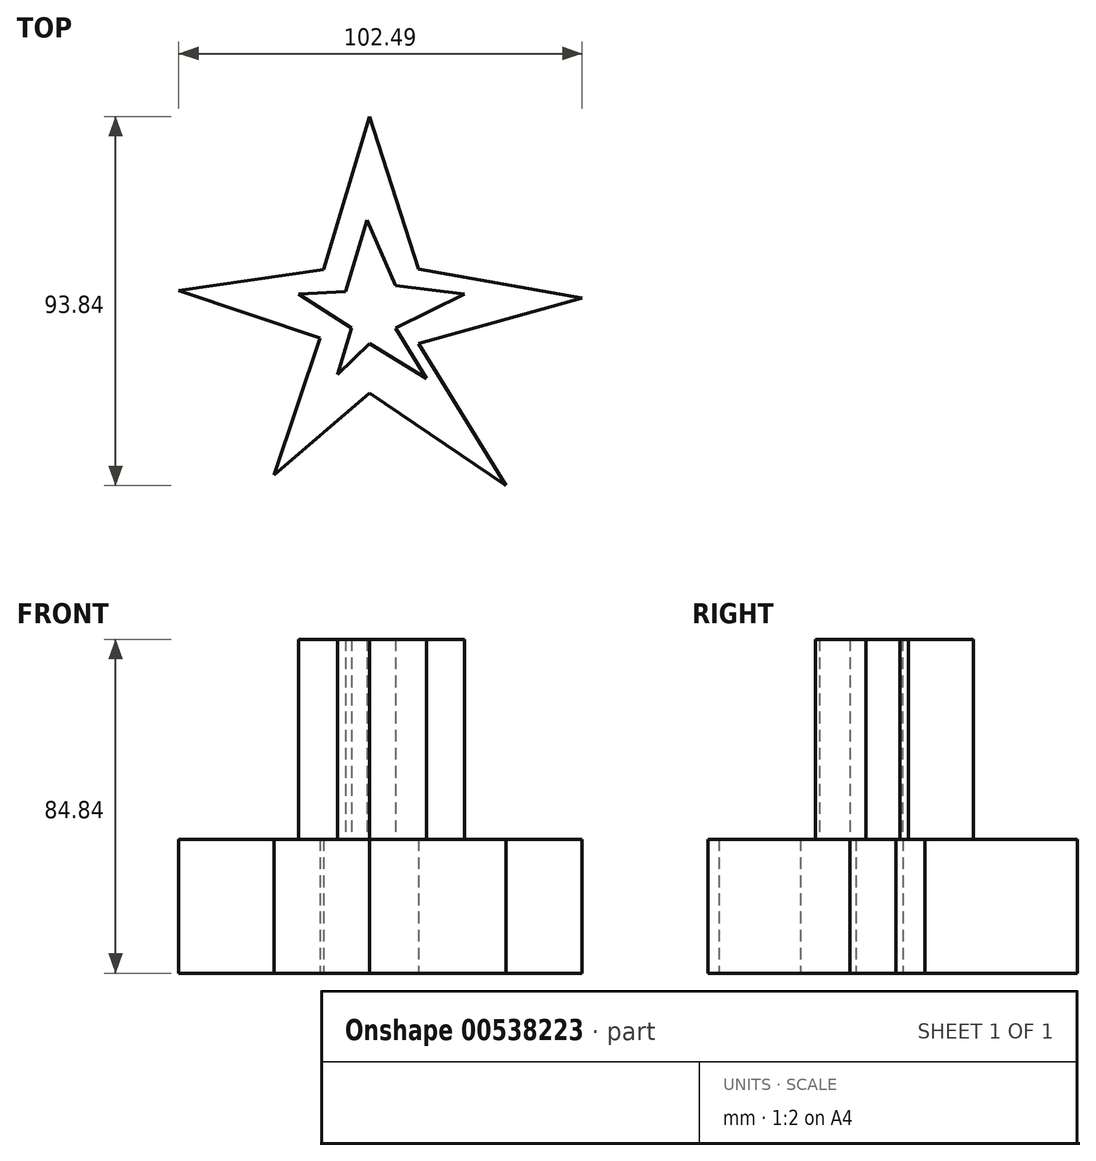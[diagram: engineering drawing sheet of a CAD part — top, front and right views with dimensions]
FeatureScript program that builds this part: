
annotation { "Feature Type Name" : "Feature", "Feature Type Description" : "" }
export const myFeature = defineFeature(function(context is Context, id is Id, definition is map)
    precondition{}
    {
        {
            var Q0;
            Q0=qCreatedBy(makeId("Top.planeOp"),FACE);
            var sketch = newSketch(context, id + "F0", { "sketchPlane" : qUnion([Q0])});
            skLineSegment(sketch, "E0", {"start": v(-62.37, 44.98) * mm, "end": v(-62.37, 49.04) * mm});
            skLineSegment(sketch, "E1", {"start": v(-11.71, 23.03) * mm, "end": v(0, 61.94) * mm});
            skLineSegment(sketch, "E2", {"start": v(0, 61.94) * mm, "end": v(12.43, 23.2) * mm});
            skLineSegment(sketch, "E3", {"start": v(12.43, 23.2) * mm, "end": v(54.01, 15.77) * mm});
            skLineSegment(sketch, "E4", {"start": v(54.01, 15.77) * mm, "end": v(12.43, 4.18) * mm});
            skLineSegment(sketch, "E5", {"start": v(12.43, 4.18) * mm, "end": v(34.64, -31.9) * mm});
            skLineSegment(sketch, "E6", {"start": v(34.64, -31.9) * mm, "end": v(0, -8.39) * mm});
            skLineSegment(sketch, "E7", {"start": v(0, -8.39) * mm, "end": v(-24.2, -29.13) * mm});
            skLineSegment(sketch, "E8", {"start": v(-24.2, -29.13) * mm, "end": v(-12.56, 5.63) * mm});
            skLineSegment(sketch, "E9", {"start": v(-12.56, 5.63) * mm, "end": v(-48.48, 17.66) * mm});
            skLineSegment(sketch, "E10", {"start": v(-48.48, 17.66) * mm, "end": v(-11.71, 23.03) * mm});
            skSolve(sketch);
        }
        {
            var Q0;
            Q0=makeQuery(id+"F0.imprint","IMPRINT",FACE,{"disambiguationData":[TD([[makeQuery(id+"F0.imprint","IMPRINT",EDGE,{"derivedFrom":sQuery(id+"F0.wireOp",EDGE,"E1")}),-1.0]])]});
            extrude(context, id + "F1", {"entities" : qUnion([Q0]), "depth" : 34.04 * mm, "offsetDistance" : 25.4 * mm});
        }
        {
            var Q0;
            Q0=makeQuery(id+"F1.opExtrude","CAP_FACE",FACE,{"disambiguationData":[OSD([sQuery(id+"F0.wireOp",EDGE,"E1"),sQuery(id+"F0.wireOp",EDGE,"E2"),sQuery(id+"F0.wireOp",EDGE,"E3"),sQuery(id+"F0.wireOp",EDGE,"E4"),sQuery(id+"F0.wireOp",EDGE,"E5"),sQuery(id+"F0.wireOp",EDGE,"E6"),sQuery(id+"F0.wireOp",EDGE,"E7"),sQuery(id+"F0.wireOp",EDGE,"E8"),sQuery(id+"F0.wireOp",EDGE,"E9"),sQuery(id+"F0.wireOp",EDGE,"E10")])],"isStart":false});
            var sketch = newSketch(context, id + "F2", { "sketchPlane" : qUnion([Q0])});
            skLineSegment(sketch, "E11", {"start": v(-6.1, 17.4) * mm, "end": v(-0.65, 35.53) * mm});
            skLineSegment(sketch, "E12", {"start": v(-0.65, 35.53) * mm, "end": v(6.58, 19.01) * mm});
            skLineSegment(sketch, "E13", {"start": v(6.58, 19.01) * mm, "end": v(24.17, 16.78) * mm});
            skLineSegment(sketch, "E14", {"start": v(24.17, 16.78) * mm, "end": v(6.58, 8.21) * mm});
            skLineSegment(sketch, "E15", {"start": v(6.58, 8.21) * mm, "end": v(14.48, -4.62) * mm});
            skLineSegment(sketch, "E16", {"start": v(14.48, -4.62) * mm, "end": v(0, 4.18) * mm});
            skLineSegment(sketch, "E17", {"start": v(0, 4.18) * mm, "end": v(-8.1, -3.6) * mm});
            skLineSegment(sketch, "E18", {"start": v(-8.1, -3.6) * mm, "end": v(-4.55, 8.21) * mm});
            skLineSegment(sketch, "E19", {"start": v(-4.55, 8.21) * mm, "end": v(-17.98, 16.78) * mm});
            skLineSegment(sketch, "E20", {"start": v(-17.98, 16.78) * mm, "end": v(-6.1, 17.4) * mm});
            skSolve(sketch);
        }
        {
            var Q0;
            Q0=makeQuery(id+"F2.imprint","IMPRINT",FACE,{"disambiguationData":[TD([[makeQuery(id+"F2.imprint","IMPRINT",EDGE,{"derivedFrom":sQuery(id+"F2.wireOp",EDGE,"E11")}),-1.0]])]});
            extrude(context, id + "F3", {"entities" : qUnion([Q0]), "operationType" : NewBodyOperationType.ADD, "depth" : 25.4 * mm, "offsetDistance" : 25.4 * mm});
        }
        {
            var Q0;
            Q0=makeQuery(id+"F3.opExtrude","CAP_FACE",FACE,{"disambiguationData":[OSD([sQuery(id+"F2.wireOp",EDGE,"E11"),sQuery(id+"F2.wireOp",EDGE,"E12"),sQuery(id+"F2.wireOp",EDGE,"E13"),sQuery(id+"F2.wireOp",EDGE,"E14"),sQuery(id+"F2.wireOp",EDGE,"E15"),sQuery(id+"F2.wireOp",EDGE,"E16"),sQuery(id+"F2.wireOp",EDGE,"E17"),sQuery(id+"F2.wireOp",EDGE,"E18"),sQuery(id+"F2.wireOp",EDGE,"E19"),sQuery(id+"F2.wireOp",EDGE,"E20")])],"isStart":false});
            var Q1;
            Q1=makeQuery(id+"F1.opExtrude","CAP_FACE",FACE,{"disambiguationData":[OSD([sQuery(id+"F0.wireOp",EDGE,"E1"),sQuery(id+"F0.wireOp",EDGE,"E2"),sQuery(id+"F0.wireOp",EDGE,"E3"),sQuery(id+"F0.wireOp",EDGE,"E4"),sQuery(id+"F0.wireOp",EDGE,"E5"),sQuery(id+"F0.wireOp",EDGE,"E6"),sQuery(id+"F0.wireOp",EDGE,"E7"),sQuery(id+"F0.wireOp",EDGE,"E8"),sQuery(id+"F0.wireOp",EDGE,"E9"),sQuery(id+"F0.wireOp",EDGE,"E10")])],"isStart":true});
            extrude(context, id + "F4", {"entities" : qUnion([Q0, Q1]), "operationType" : NewBodyOperationType.ADD, "depth" : 25.4 * mm, "offsetDistance" : 25.4 * mm});
        }
    });
